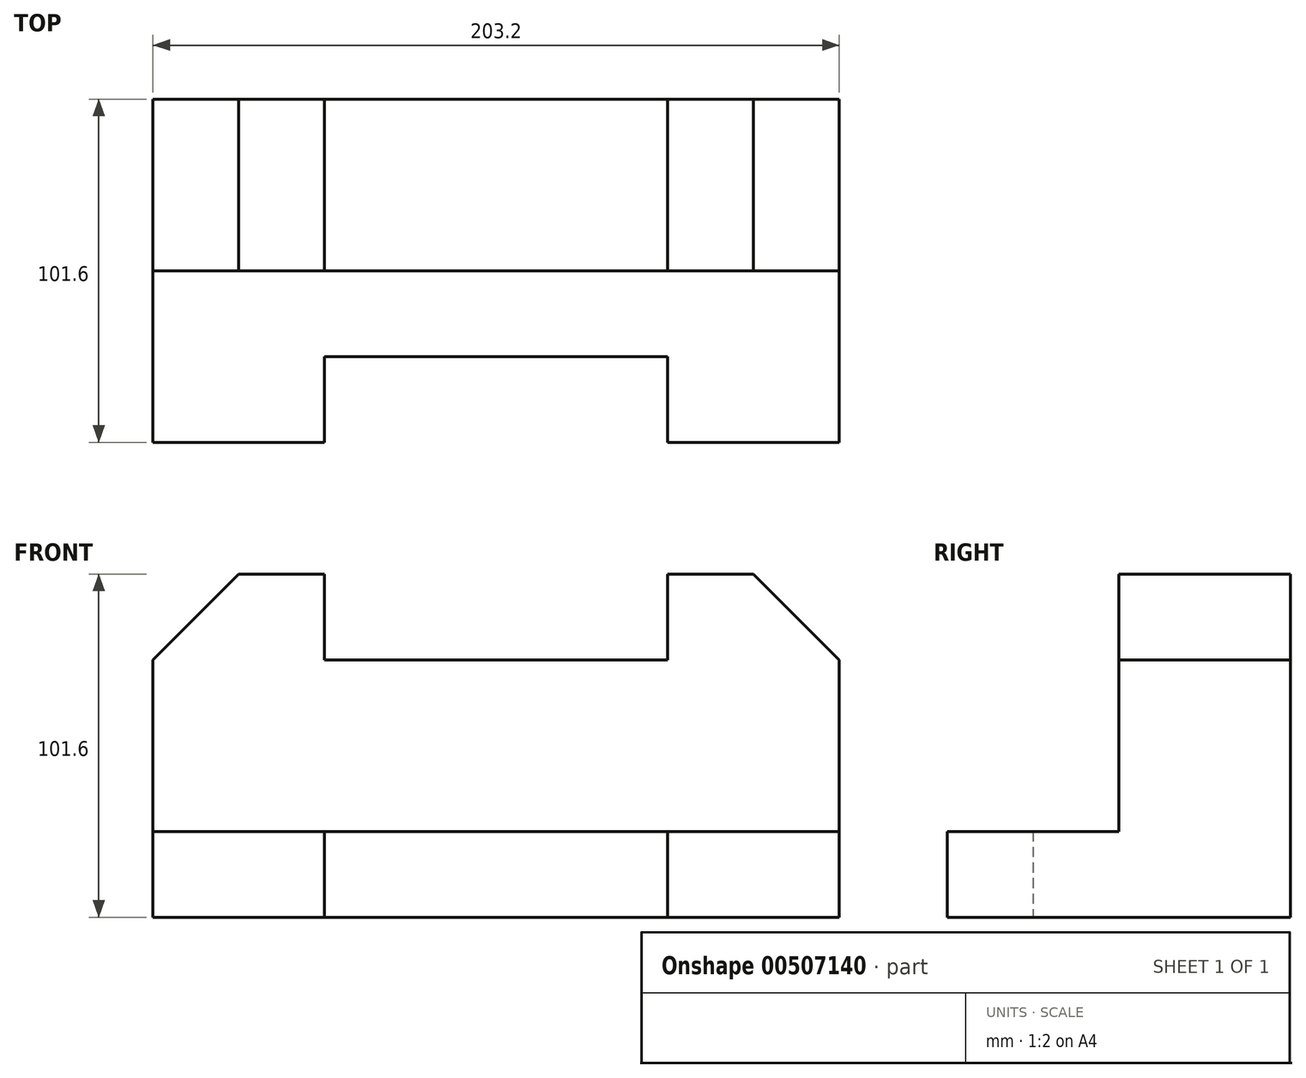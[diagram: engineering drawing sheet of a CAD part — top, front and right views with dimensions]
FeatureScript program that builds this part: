
annotation { "Feature Type Name" : "Feature", "Feature Type Description" : "" }
export const myFeature = defineFeature(function(context is Context, id is Id, definition is map)
    precondition{}
    {
        {
            var Q0;
            Q0=qCreatedBy(makeId("Top.planeOp"),FACE);
            var sketch = newSketch(context, id + "F0", { "sketchPlane" : qUnion([Q0])});
            skLineSegment(sketch, "E0.bottom", {"start": v(101.6, 50.8) * mm, "end": v(-101.6, 50.8) * mm});
            skLineSegment(sketch, "E0.top", {"start": v(101.6, -50.8) * mm, "end": v(-101.6, -50.8) * mm});
            skLineSegment(sketch, "E0.left", {"start": v(101.6, 50.8) * mm, "end": v(101.6, -50.8) * mm});
            skLineSegment(sketch, "E0.right", {"start": v(-101.6, 50.8) * mm, "end": v(-101.6, -50.8) * mm});
            skPoint(sketch, "E0.middle", {"position": v(0, 0) * mm});
            skLineSegment(sketch, "E1.bottom", {"start": v(-50.8, -50.8) * mm, "end": v(50.8, -50.8) * mm});
            skLineSegment(sketch, "E1.top", {"start": v(-50.8, -25.4) * mm, "end": v(50.8, -25.4) * mm});
            skLineSegment(sketch, "E1.left", {"start": v(-50.8, -50.8) * mm, "end": v(-50.8, -25.4) * mm});
            skLineSegment(sketch, "E1.right", {"start": v(50.8, -50.8) * mm, "end": v(50.8, -25.4) * mm});
            skSolve(sketch);
        }
        {
            var Q0;
            Q0=makeQuery(id+"F0.imprint","IMPRINT",FACE,{"disambiguationData":[TD([[makeQuery(id+"F0.imprint","IMPRINT",EDGE,{"derivedFrom":sQuery(id+"F0.wireOp",EDGE,"E0.bottom")}),1.0]])]});
            extrude(context, id + "F1", {"entities" : qUnion([Q0]), "depth" : 25.4 * mm});
        }
        {
            var Q0;
            Q0=makeQuery(id+"F1.opExtrude","CAP_FACE",FACE,{"disambiguationData":[OSD([sQuery(id+"F0.wireOp",EDGE,"E0.bottom"),sQuery(id+"F0.wireOp",EDGE,"E0.top"),sQuery(id+"F0.wireOp",EDGE,"E0.left"),sQuery(id+"F0.wireOp",EDGE,"E0.right"),sQuery(id+"F0.wireOp",EDGE,"E1.top"),sQuery(id+"F0.wireOp",EDGE,"E1.left"),sQuery(id+"F0.wireOp",EDGE,"E1.right")])],"isStart":false});
            var sketch = newSketch(context, id + "F2", { "sketchPlane" : qUnion([Q0])});
            skLineSegment(sketch, "E2.bottom", {"start": v(-101.6, 50.8) * mm, "end": v(101.6, 50.8) * mm});
            skLineSegment(sketch, "E2.top", {"start": v(-101.6, 0) * mm, "end": v(101.6, 0) * mm});
            skLineSegment(sketch, "E2.left", {"start": v(-101.6, 50.8) * mm, "end": v(-101.6, 0) * mm});
            skLineSegment(sketch, "E2.right", {"start": v(101.6, 50.8) * mm, "end": v(101.6, 0) * mm});
            skSolve(sketch);
        }
        {
            var Q0;
            Q0=makeQuery(id+"F2.imprint","IMPRINT",FACE,{"disambiguationData":[TD([[makeQuery(id+"F2.imprint","IMPRINT",EDGE,{"derivedFrom":sQuery(id+"F2.wireOp",EDGE,"E2.bottom")}),1.0]])]});
            extrude(context, id + "F3", {"entities" : qUnion([Q0]), "operationType" : NewBodyOperationType.ADD, "depth" : 76.2 * mm});
        }
        {
            var Q0;
            Q0=makeQuery(id+"F3.opExtrude","CAP_FACE",FACE,{"disambiguationData":[OSD([sQuery(id+"F2.wireOp",EDGE,"E2.bottom"),sQuery(id+"F2.wireOp",EDGE,"E2.top"),sQuery(id+"F2.wireOp",EDGE,"E2.left"),sQuery(id+"F2.wireOp",EDGE,"E2.right")])],"isStart":false});
            var sketch = newSketch(context, id + "F4", { "sketchPlane" : qUnion([Q0])});
            skLineSegment(sketch, "E3.bottom", {"start": v(-50.8, 50.8) * mm, "end": v(50.8, 50.8) * mm});
            skLineSegment(sketch, "E3.top", {"start": v(-50.8, 0) * mm, "end": v(50.8, 0) * mm});
            skLineSegment(sketch, "E3.left", {"start": v(-50.8, 50.8) * mm, "end": v(-50.8, 0) * mm});
            skLineSegment(sketch, "E3.right", {"start": v(50.8, 50.8) * mm, "end": v(50.8, 0) * mm});
            skSolve(sketch);
        }
        {
            var Q0;
            Q0 = qSketchRegion(id + "F4", true);
            extrude(context, id + "F5", {"entities" : qUnion([Q0]), "operationType" : NewBodyOperationType.REMOVE, "oppositeDirection" : true, "depth" : 25.4 * mm});
        }
        {
            var Q0;
            Q0=makeQuery(id+"F3.opExtrude","SWEPT_FACE",FACE,{"disambiguationData":[OSD([sQuery(id+"F2.wireOp",EDGE,"E2.top")])]});
            var sketch = newSketch(context, id + "F6", { "sketchPlane" : qUnion([Q0])});
            skLineSegment(sketch, "E4", {"start": v(76.2, 101.6) * mm, "end": v(101.6, 101.6) * mm});
            skLineSegment(sketch, "E5", {"start": v(101.6, 101.6) * mm, "end": v(101.6, 76.2) * mm});
            skLineSegment(sketch, "E6", {"start": v(101.6, 76.2) * mm, "end": v(76.2, 101.6) * mm});
            skSolve(sketch);
        }
        {
            var Q0;
            Q0=makeQuery(id+"F6.imprint","IMPRINT",FACE,{"disambiguationData":[TD([[makeQuery(id+"F6.imprint","IMPRINT",EDGE,{"derivedFrom":sQuery(id+"F6.wireOp",EDGE,"E4")}),-1.0]])]});
            extrude(context, id + "F7", {"entities" : qUnion([Q0]), "operationType" : NewBodyOperationType.REMOVE, "oppositeDirection" : true, "depth" : 50.8 * mm});
        }
        {
            var Q0;
            Q0=makeQuery(id+"F3.opExtrude","SWEPT_FACE",FACE,{"disambiguationData":[OSD([sQuery(id+"F2.wireOp",EDGE,"E2.top")])]});
            var sketch = newSketch(context, id + "F8", { "sketchPlane" : qUnion([Q0])});
            skLineSegment(sketch, "E7", {"start": v(-76.2, 101.6) * mm, "end": v(-101.6, 101.6) * mm});
            skLineSegment(sketch, "E8", {"start": v(-101.6, 101.6) * mm, "end": v(-101.6, 76.2) * mm});
            skLineSegment(sketch, "E9", {"start": v(-101.6, 76.2) * mm, "end": v(-76.2, 101.6) * mm});
            skSolve(sketch);
        }
        {
            var Q0;
            Q0=makeQuery(id+"F8.imprint","IMPRINT",FACE,{"disambiguationData":[TD([[makeQuery(id+"F8.imprint","IMPRINT",EDGE,{"derivedFrom":sQuery(id+"F8.wireOp",EDGE,"E7")}),-1.0]])]});
            extrude(context, id + "F9", {"entities" : qUnion([Q0]), "operationType" : NewBodyOperationType.REMOVE, "oppositeDirection" : true, "depth" : 50.8 * mm});
        }
    });
